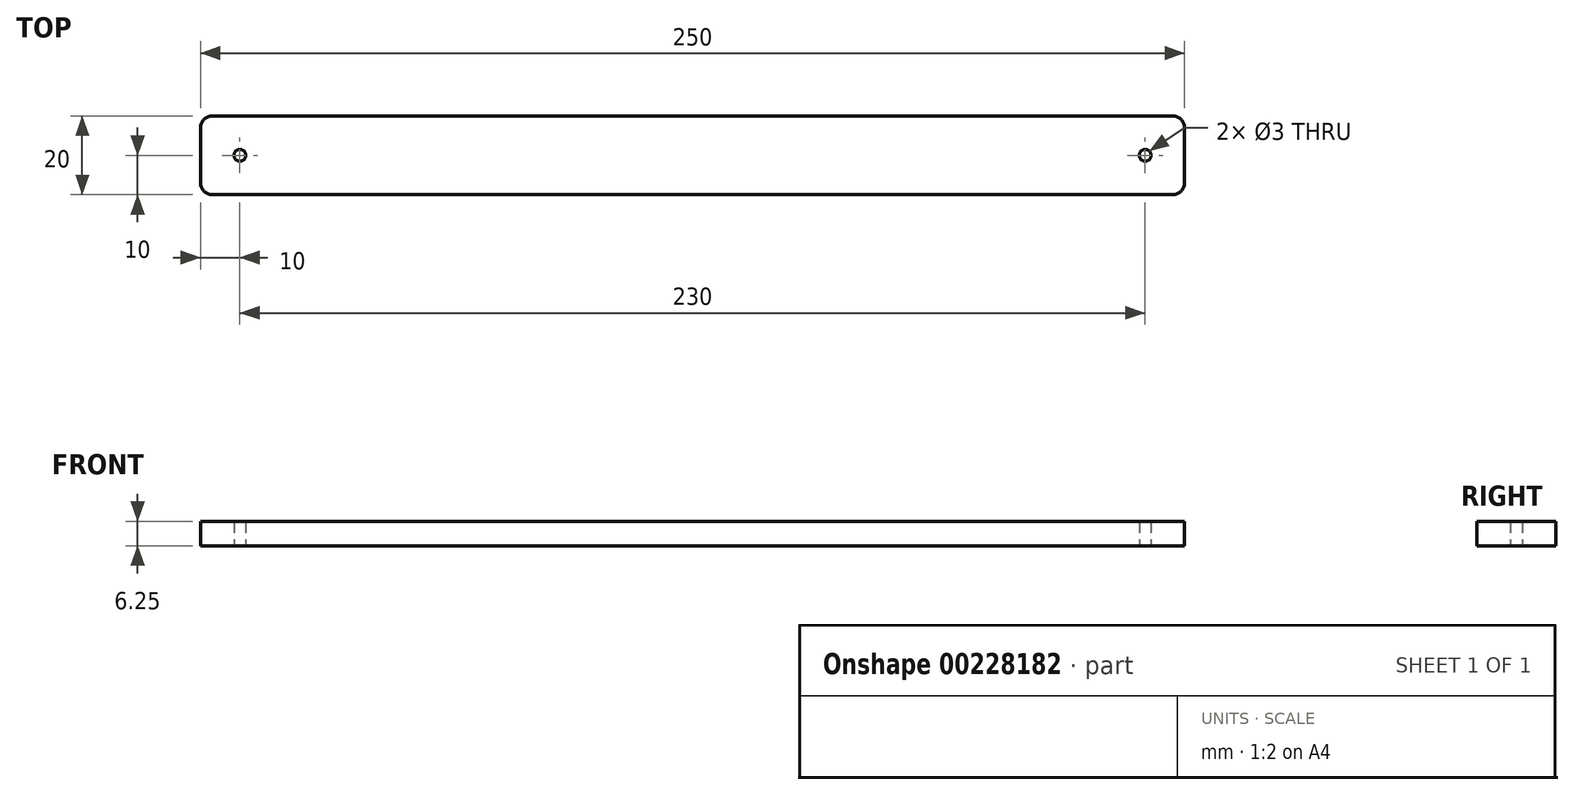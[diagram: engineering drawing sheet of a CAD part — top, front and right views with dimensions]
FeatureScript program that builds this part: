
annotation { "Feature Type Name" : "Feature", "Feature Type Description" : "" }
export const myFeature = defineFeature(function(context is Context, id is Id, definition is map)
    precondition{}
    {
        {
            var Q0;
            Q0=qCreatedBy(makeId("Top.planeOp"),FACE);
            var sketch = newSketch(context, id + "F0", { "sketchPlane" : qUnion([Q0])});
            skCircle(sketch, "E0", {"center": v(0, 0) * mm, "radius": 1.5 * mm});
            skCircle(sketch, "E1", {"center": v(230, 0) * mm, "radius": 1.5 * mm});
            skLineSegment(sketch, "E2.bottom", {"start": v(-7, 10) * mm, "end": v(237, 10) * mm});
            skLineSegment(sketch, "E2.top", {"start": v(-7, -10) * mm, "end": v(237, -10) * mm});
            skLineSegment(sketch, "E2.left", {"start": v(-10, 7) * mm, "end": v(-10, -7) * mm});
            skLineSegment(sketch, "E2.right", {"start": v(240, 7) * mm, "end": v(240, -7) * mm});
            skPoint(sketch, "E3.visualSharp", {"position": v(240, 10) * mm});
            skArc(sketch, "E3.filletArc", {"start": v(240, 7) * mm, "mid": v(239.12, 9.12) * mm, "end": v(237, 10) * mm});
            skPoint(sketch, "E4.visualSharp", {"position": v(240, -10) * mm});
            skArc(sketch, "E4.filletArc", {"start": v(237, -10) * mm, "mid": v(239.12, -9.12) * mm, "end": v(240, -7) * mm});
            skPoint(sketch, "E5.visualSharp", {"position": v(-10, -10) * mm});
            skArc(sketch, "E5.filletArc", {"start": v(-10, -7) * mm, "mid": v(-9.12, -9.12) * mm, "end": v(-7, -10) * mm});
            skPoint(sketch, "E6.visualSharp", {"position": v(-10, 10) * mm});
            skArc(sketch, "E6.filletArc", {"start": v(-7, 10) * mm, "mid": v(-9.12, 9.12) * mm, "end": v(-10, 7) * mm});
            skSolve(sketch);
        }
        {
            var Q0;
            Q0 = qSketchRegion(id + "F0", true);
            extrude(context, id + "F1", {"entities" : qUnion([Q0]), "depth" : (12.5 / 2) * mm});
        }
    });
